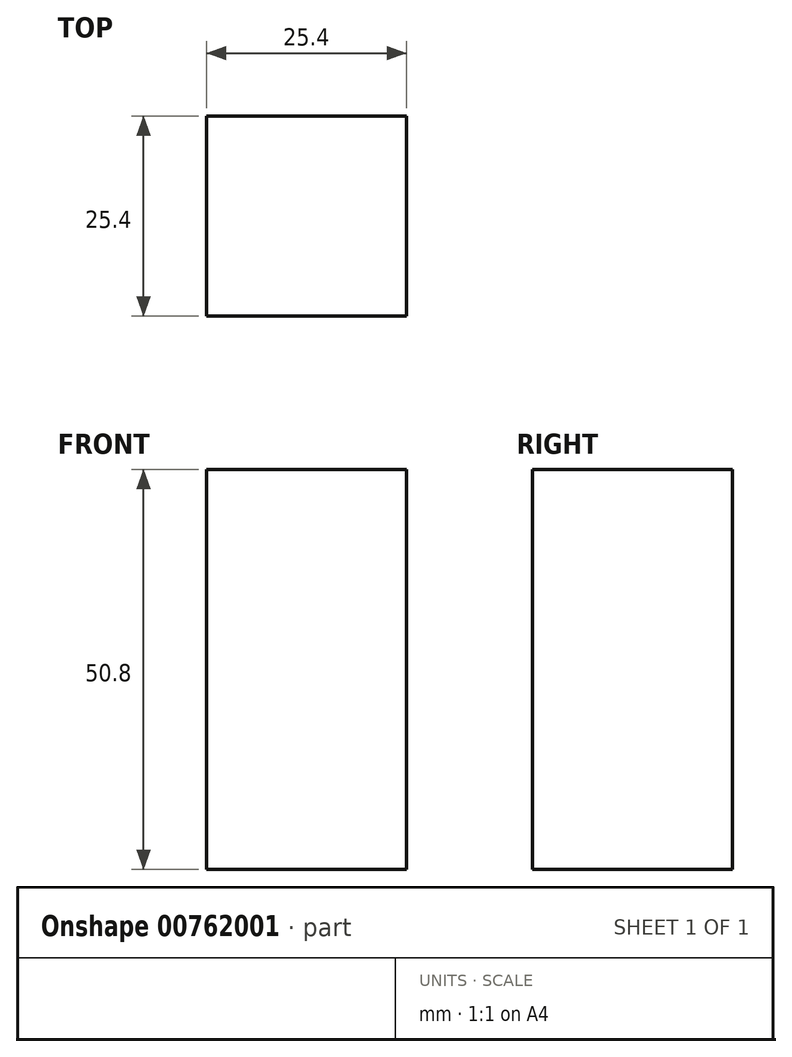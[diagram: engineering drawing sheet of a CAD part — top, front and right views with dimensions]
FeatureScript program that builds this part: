
annotation { "Feature Type Name" : "Feature", "Feature Type Description" : "" }
export const myFeature = defineFeature(function(context is Context, id is Id, definition is map)
    precondition{}
    {
        {
            var Q0;
            Q0=qCreatedBy(makeId("Top.planeOp"),FACE);
            var sketch = newSketch(context, id + "F0", { "sketchPlane" : qUnion([Q0])});
            skLineSegment(sketch, "E0.bottom", {"start": v(4.23, 0) * mm, "end": v(29.63, 0) * mm});
            skLineSegment(sketch, "E0.top", {"start": v(4.23, -25.4) * mm, "end": v(29.63, -25.4) * mm});
            skLineSegment(sketch, "E0.left", {"start": v(4.23, 0) * mm, "end": v(4.23, -25.4) * mm});
            skLineSegment(sketch, "E0.right", {"start": v(29.63, 0) * mm, "end": v(29.63, -25.4) * mm});
            skSolve(sketch);
        }
        {
            var Q0;
            Q0=makeQuery(id+"F0.imprint","IMPRINT",FACE,{"disambiguationData":[TD([[makeQuery(id+"F0.imprint","IMPRINT",EDGE,{"derivedFrom":sQuery(id+"F0.wireOp",EDGE,"E0.bottom")}),-1.0]])]});
            extrude(context, id + "F1", {"entities" : qUnion([Q0]), "depth" : 50.8 * mm, "offsetDistance" : 25.4 * mm});
        }
    });
